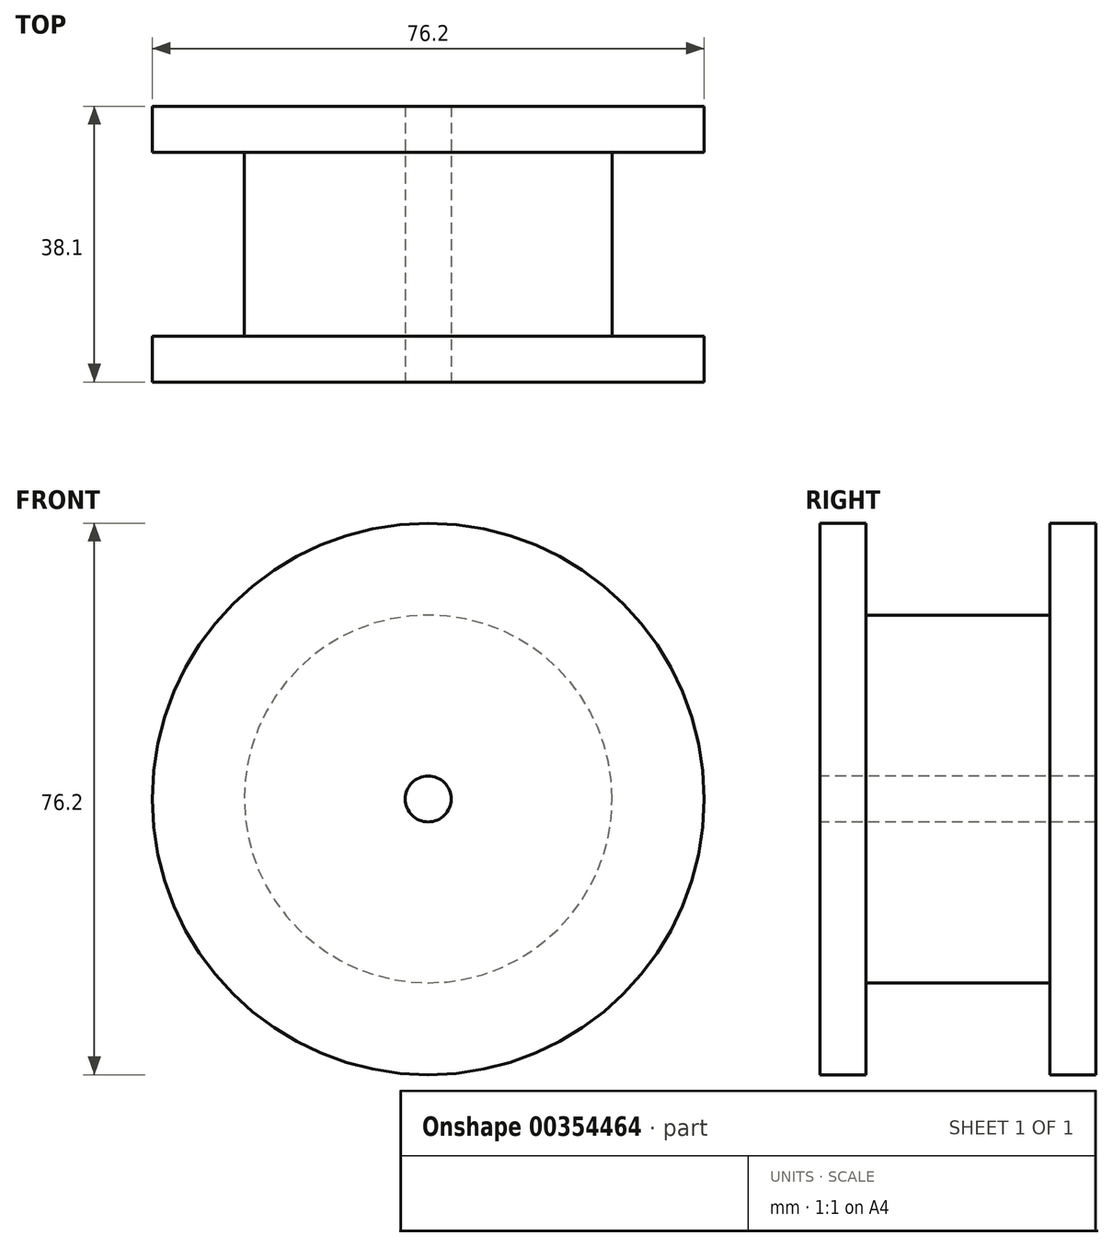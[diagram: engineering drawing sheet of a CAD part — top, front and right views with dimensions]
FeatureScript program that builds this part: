
annotation { "Feature Type Name" : "Feature", "Feature Type Description" : "" }
export const myFeature = defineFeature(function(context is Context, id is Id, definition is map)
    precondition{}
    {
        {
            var Q0;
            Q0=qCreatedBy(makeId("Front.planeOp"),FACE);
            var sketch = newSketch(context, id + "F0", { "sketchPlane" : qUnion([Q0])});
            skCircle(sketch, "E0", {"center": v(0, 0) * mm, "radius": 38.1 * mm});
            skSolve(sketch);
        }
        {
            var Q0;
            Q0=makeQuery(id+"F0.imprint","IMPRINT",FACE,{"disambiguationData":[TD([[makeQuery(id+"F0.imprint","IMPRINT",EDGE,{"derivedFrom":sQuery(id+"F0.wireOp",EDGE,"E0")}),1.0]])]});
            extrude(context, id + "F1", {"entities" : qUnion([Q0]), "depth" : 6.35 * mm});
        }
        {
            var Q0;
            Q0=makeQuery(id+"F1.opExtrude","CAP_FACE",FACE,{"disambiguationData":[OSD([sQuery(id+"F0.wireOp",EDGE,"E0")])],"isStart":false});
            var sketch = newSketch(context, id + "F2", { "sketchPlane" : qUnion([Q0])});
            skCircle(sketch, "E1", {"center": v(0, 0) * mm, "radius": 25.4 * mm});
            skSolve(sketch);
        }
        {
            var Q0;
            Q0=makeQuery(id+"F2.imprint","IMPRINT",FACE,{"disambiguationData":[TD([[makeQuery(id+"F2.imprint","IMPRINT",EDGE,{"derivedFrom":sQuery(id+"F2.wireOp",EDGE,"E1")}),1.0]])]});
            extrude(context, id + "F3", {"entities" : qUnion([Q0]), "operationType" : NewBodyOperationType.ADD, "depth" : 25.4 * mm});
        }
        {
            var Q0;
            Q0=makeQuery(id+"F3.opExtrude","CAP_FACE",FACE,{"disambiguationData":[OSD([sQuery(id+"F2.wireOp",EDGE,"E1")])],"isStart":false});
            var sketch = newSketch(context, id + "F4", { "sketchPlane" : qUnion([Q0])});
            skCircle(sketch, "E2", {"center": v(0, 0) * mm, "radius": 38.1 * mm});
            skSolve(sketch);
        }
        {
            var Q0;
            Q0=makeQuery(id+"F4.imprint","IMPRINT",FACE,{"disambiguationData":[TD([[makeQuery(id+"F4.imprint","IMPRINT",EDGE,{"derivedFrom":makeQuery(id+"F3.opExtrude","CAP_EDGE",EDGE,{"disambiguationData":[OSD([sQuery(id+"F2.wireOp",EDGE,"E1")])],"isStart":false})}),1.0]])]});
            var Q1;
            Q1=makeQuery(id+"F4.imprint","IMPRINT",FACE,{"disambiguationData":[TD([[makeQuery(id+"F4.imprint","IMPRINT",EDGE,{"derivedFrom":sQuery(id+"F4.wireOp",EDGE,"E2")}),1.0]])]});
            extrude(context, id + "F5", {"entities" : qUnion([Q0, Q1]), "operationType" : NewBodyOperationType.ADD, "depth" : 6.35 * mm});
        }
        {
            var Q0;
            Q0=makeQuery(id+"F5.opExtrude","CAP_FACE",FACE,{"disambiguationData":[OSD([sQuery(id+"F4.wireOp",EDGE,"E2")])],"isStart":false});
            var sketch = newSketch(context, id + "F6", { "sketchPlane" : qUnion([Q0])});
            skCircle(sketch, "E3", {"center": v(0, 0) * mm, "radius": 3.18 * mm});
            skSolve(sketch);
        }
        {
            var Q0;
            Q0=makeQuery(id+"F6.imprint","IMPRINT",FACE,{"disambiguationData":[TD([[makeQuery(id+"F6.imprint","IMPRINT",EDGE,{"derivedFrom":sQuery(id+"F6.wireOp",EDGE,"E3")}),1.0]])]});
            extrude(context, id + "F7", {"entities" : qUnion([Q0]), "operationType" : NewBodyOperationType.REMOVE, "endBound" : BoundingType.THROUGH_ALL, "oppositeDirection" : true, "depth" : 25.4 * mm});
        }
    });
